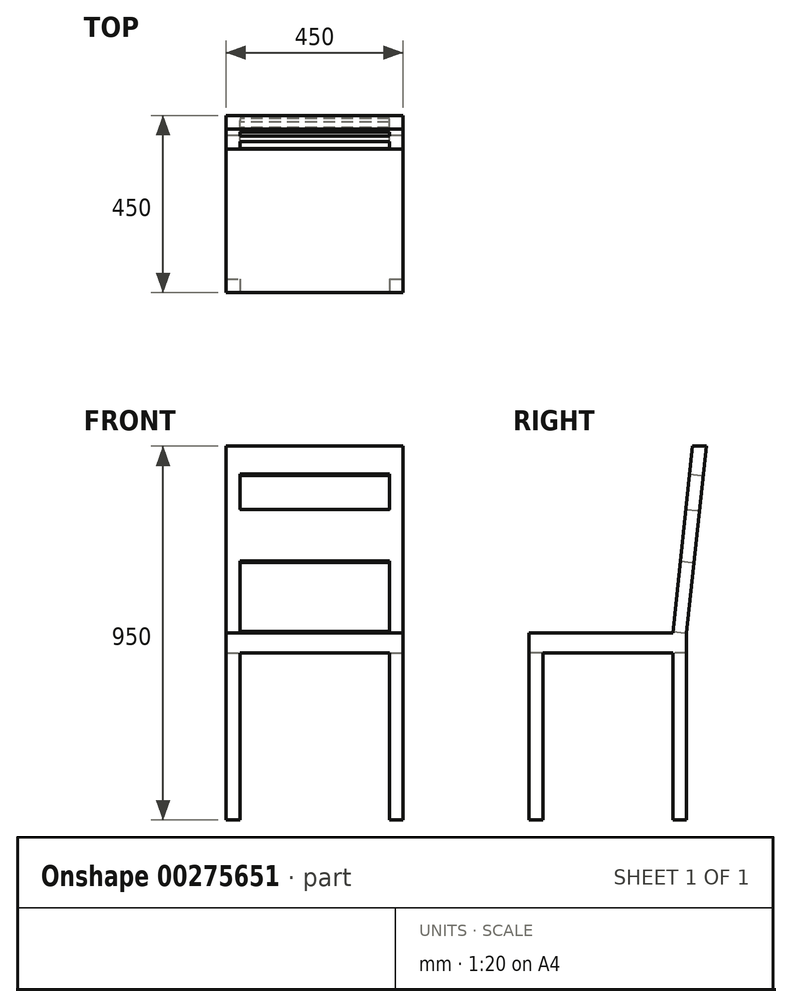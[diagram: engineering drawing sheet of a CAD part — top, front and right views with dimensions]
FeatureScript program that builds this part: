
annotation { "Feature Type Name" : "Feature", "Feature Type Description" : "" }
export const myFeature = defineFeature(function(context is Context, id is Id, definition is map)
    precondition{}
    {
        {
            var Q0;
            Q0=qCreatedBy(makeId("Top.planeOp"),FACE);
            var sketch = newSketch(context, id + "F0", { "sketchPlane" : qUnion([Q0])});
            skLineSegment(sketch, "E0.bottom", {"start": v(225, 225) * mm, "end": v(-225, 225) * mm});
            skLineSegment(sketch, "E0.top", {"start": v(225, -225) * mm, "end": v(-225, -225) * mm});
            skLineSegment(sketch, "E0.left", {"start": v(225, 225) * mm, "end": v(225, -225) * mm});
            skLineSegment(sketch, "E0.right", {"start": v(-225, 225) * mm, "end": v(-225, -225) * mm});
            skPoint(sketch, "E0.middle", {"position": v(0, 0) * mm});
            skSolve(sketch);
        }
        {
            var Q0;
            Q0=qSketchRegion(id+"F0",true);
            extrude(context, id + "F1", {"entities" : qUnion([Q0]), "depth" : 950 * mm});
        }
        {
            var Q0;
            Q0=makeQuery(id+"F1.opExtrude","SWEPT_FACE",FACE,{"disambiguationData":[OSD([sQuery(id+"F0.wireOp",EDGE,"E0.left")])]});
            var sketch = newSketch(context, id + "F2", { "sketchPlane" : qUnion([Q0])});
            skLineSegment(sketch, "E1.bottom", {"start": v(225, 475) * mm, "end": v(-225, 475) * mm});
            skLineSegment(sketch, "E1.top", {"start": v(225, 425) * mm, "end": v(-225, 425) * mm});
            skLineSegment(sketch, "E1.left", {"start": v(225, 475) * mm, "end": v(225, 425) * mm});
            skLineSegment(sketch, "E1.right", {"start": v(-225, 475) * mm, "end": v(-225, 425) * mm});
            skLineSegment(sketch, "E2", {"start": v(225, 950) * mm, "end": v(175, 475) * mm});
            skLineSegment(sketch, "E3", {"start": v(175, 475) * mm, "end": v(225, 475) * mm});
            skLineSegment(sketch, "E4", {"start": v(190, 950) * mm, "end": v(140, 475) * mm});
            skLineSegment(sketch, "E5", {"start": v(175, 475) * mm, "end": v(175, 0) * mm});
            skLineSegment(sketch, "E6", {"start": v(140, 475) * mm, "end": v(140, 0) * mm});
            skLineSegment(sketch, "E7.bottom", {"start": v(-225, 425) * mm, "end": v(-190, 425) * mm});
            skLineSegment(sketch, "E7.top", {"start": v(-225, 0) * mm, "end": v(-190, 0) * mm});
            skLineSegment(sketch, "E7.left", {"start": v(-225, 425) * mm, "end": v(-225, 0) * mm});
            skLineSegment(sketch, "E7.right", {"start": v(-190, 425) * mm, "end": v(-190, 0) * mm});
            skSolve(sketch);
        }
        {
            var Q0;
            {var subQ0=sQuery(id+"F2.wireOp",EDGE,"E1.left");Q0=makeQuery(id+"F2.imprint","IMPRINT",FACE,{"disambiguationData":[TD([[makeQuery(id+"F2.imprint","IMPRINT",EDGE,{"derivedFrom":subQ0}),-1.0]])]});}
            var Q1;
            {var subQ4=sQuery(id+"F2.wireOp",EDGE,"E4");Q1=makeQuery(id+"F2.imprint","IMPRINT",FACE,{"disambiguationData":[TD([[makeQuery(id+"F2.imprint","IMPRINT",EDGE,{"derivedFrom":subQ4}),-1.0]])]});}
            var Q2;
            {var subQ0=sQuery(id+"F2.wireOp",EDGE,"E7.right");Q2=makeQuery(id+"F2.imprint","IMPRINT",FACE,{"disambiguationData":[TD([[makeQuery(id+"F2.imprint","IMPRINT",EDGE,{"derivedFrom":subQ0}),1.0]])]});}
            var Q3;
            {var subQ1=sQuery(id+"F0.wireOp",EDGE,"E0.left");var subQ4=sQuery(id+"F2.wireOp",EDGE,"E5");var subQ6=makeQuery(id+"F1.opExtrude","CAP_EDGE",EDGE,{"disambiguationData":[OSD([subQ1])],"isStart":true});var subQ7=makeQuery(id+"F2.imprint","INTERSECT",VERTEX,{"derivedFrom":[subQ6,subQ4]});Q3=makeQuery(id+"F2.imprint","IMPRINT",FACE,{"disambiguationData":[TD([[makeQuery(id+"F2.imprint","IMPRINT",EDGE,{"disambiguationData":[TD([[subQ7,1.0]])],"derivedFrom":subQ4}),1.0]])]});}
            var Q4;
            {var subQ0=sQuery(id+"F2.wireOp",EDGE,"E2");Q4=makeQuery(id+"F2.imprint","IMPRINT",FACE,{"disambiguationData":[TD([[makeQuery(id+"F2.imprint","IMPRINT",EDGE,{"derivedFrom":subQ0}),1.0]])]});}
            extrude(context, id + "F3", {"entities" : qUnion([Q0, Q1, Q2, Q3, Q4]), "operationType" : NewBodyOperationType.REMOVE, "endBound" : BoundingType.THROUGH_ALL, "oppositeDirection" : true, "depth" : 25 * mm});
        }
        {
            var Q0;
            Q0=makeQuery(id+"F1.opExtrude","SWEPT_FACE",FACE,{"disambiguationData":[OSD([sQuery(id+"F0.wireOp",EDGE,"E0.top")])]});
            var sketch = newSketch(context, id + "F4", { "sketchPlane" : qUnion([Q0])});
            skLineSegment(sketch, "E8", {"start": v(-190, 425) * mm, "end": v(-190, 0) * mm});
            skLineSegment(sketch, "E9", {"start": v(-190, 425) * mm, "end": v(190, 425) * mm});
            skLineSegment(sketch, "E10", {"start": v(190, 425) * mm, "end": v(190, 0) * mm});
            skSolve(sketch);
        }
        {
            var Q0;
            Q0 = qSketchRegion(id + "F4", true);
            var Q1;
            {var subQ0=sQuery(id+"F4.wireOp",EDGE,"E8");Q1=makeQuery(id+"F4.imprint","IMPRINT",FACE,{"disambiguationData":[TD([[makeQuery(id+"F4.imprint","IMPRINT",EDGE,{"derivedFrom":subQ0}),1.0]])]});}
            extrude(context, id + "F5", {"entities" : qUnion([Q0, Q1]), "operationType" : NewBodyOperationType.REMOVE, "endBound" : BoundingType.THROUGH_ALL, "oppositeDirection" : true, "depth" : 25 * mm});
        }
        {
            var Q0;
            Q0=makeQuery(id+"F3.boolean.opBoolean","COPY",FACE,{"derivedFrom":makeQuery(id+"F3.opExtrude","SWEPT_FACE",FACE,{"disambiguationData":[OSD([sQuery(id+"F2.wireOp",EDGE,"E2")])]})});
            var sketch = newSketch(context, id + "F6", { "sketchPlane" : qUnion([Q0])});
            skLineSegment(sketch, "E11", {"start": v(-190, 490.7) * mm, "end": v(-190, 893.33) * mm});
            skLineSegment(sketch, "E12", {"start": v(-190, 893.33) * mm, "end": v(190, 893.33) * mm});
            skLineSegment(sketch, "E13", {"start": v(190, 893.33) * mm, "end": v(190, 490.7) * mm});
            skLineSegment(sketch, "E14", {"start": v(-190, 803.33) * mm, "end": v(190, 803.33) * mm});
            skLineSegment(sketch, "E15", {"start": v(-190, 670.7) * mm, "end": v(190, 670.7) * mm});
            skSolve(sketch);
        }
        {
            var Q0;
            {var subQ3=sQuery(id+"F6.wireOp",EDGE,"E15");Q0=makeQuery(id+"F6.imprint","IMPRINT",FACE,{"disambiguationData":[TD([[makeQuery(id+"F6.imprint","IMPRINT",EDGE,{"derivedFrom":subQ3}),-1.0]])]});}
            var Q1;
            {var subQ0=sQuery(id+"F6.wireOp",EDGE,"E12");Q1=makeQuery(id+"F6.imprint","IMPRINT",FACE,{"disambiguationData":[TD([[makeQuery(id+"F6.imprint","IMPRINT",EDGE,{"derivedFrom":subQ0}),-1.0]])]});}
            extrude(context, id + "F7", {"entities" : qUnion([Q0, Q1]), "operationType" : NewBodyOperationType.REMOVE, "endBound" : BoundingType.THROUGH_ALL, "oppositeDirection" : true, "depth" : 25 * mm});
        }
    });
